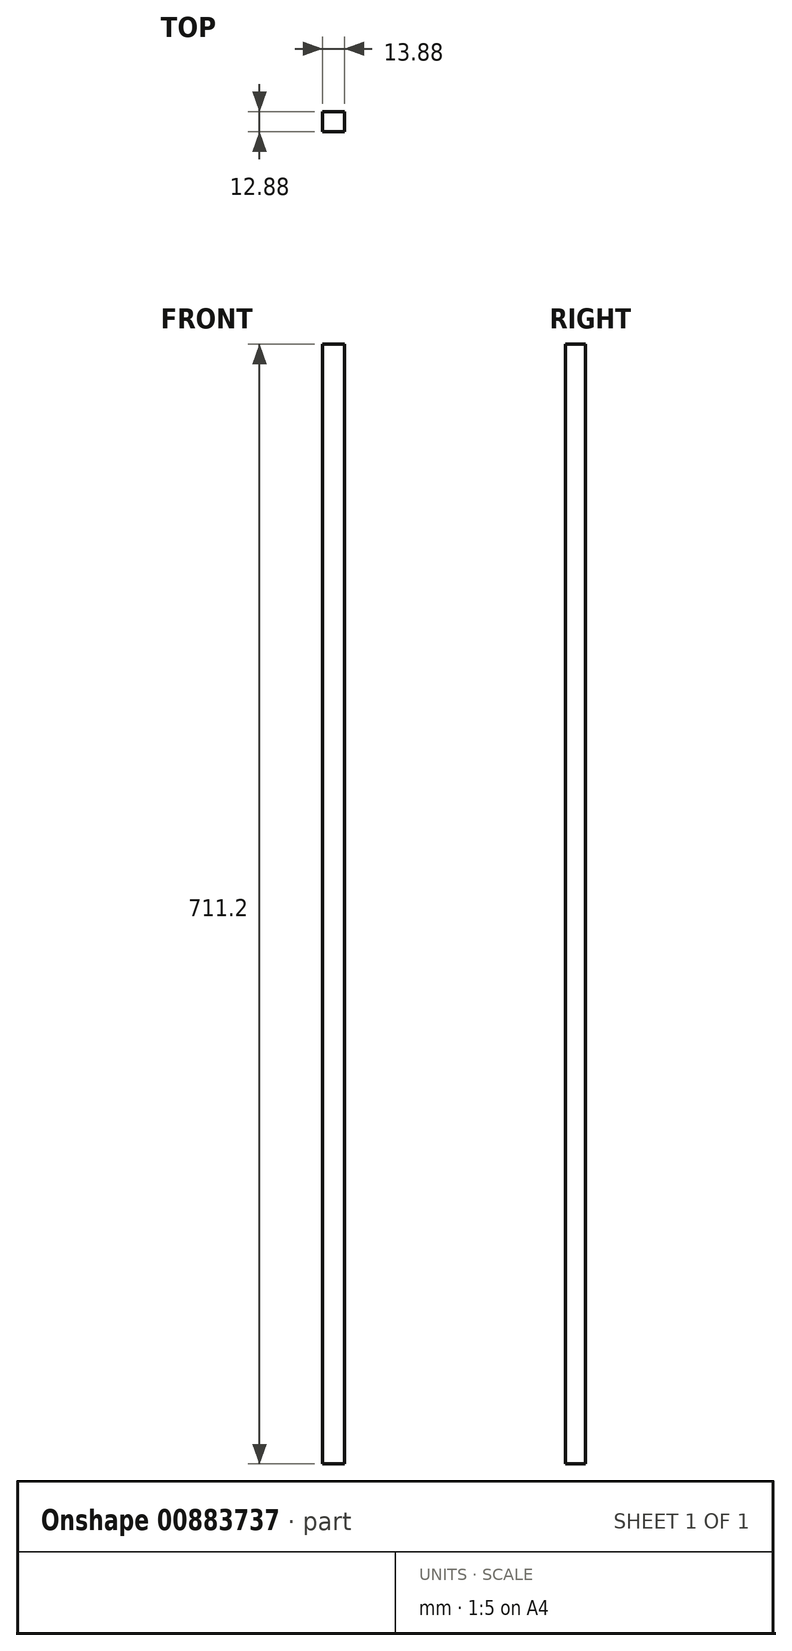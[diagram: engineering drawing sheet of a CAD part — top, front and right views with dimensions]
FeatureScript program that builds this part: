
annotation { "Feature Type Name" : "Feature", "Feature Type Description" : "" }
export const myFeature = defineFeature(function(context is Context, id is Id, definition is map)
    precondition{}
    {
        {
            var Q0;
            Q0=qCreatedBy(makeId("Top.planeOp"),FACE);
            var sketch = newSketch(context, id + "F0", { "sketchPlane" : qUnion([Q0])});
            skLineSegment(sketch, "E0.bottom", {"start": v(6.94, -6.44) * mm, "end": v(-6.94, -6.44) * mm});
            skLineSegment(sketch, "E0.top", {"start": v(6.94, 6.44) * mm, "end": v(-6.94, 6.44) * mm});
            skLineSegment(sketch, "E0.left", {"start": v(6.94, -6.44) * mm, "end": v(6.94, 6.44) * mm});
            skLineSegment(sketch, "E0.right", {"start": v(-6.94, -6.44) * mm, "end": v(-6.94, 6.44) * mm});
            skPoint(sketch, "E0.middle", {"position": v(0, 0) * mm});
            skSolve(sketch);
        }
        {
            var Q0;
            Q0=makeQuery(id+"F0.imprint","IMPRINT",FACE,{"disambiguationData":[TD([[makeQuery(id+"F0.imprint","IMPRINT",EDGE,{"derivedFrom":sQuery(id+"F0.wireOp",EDGE,"E0.bottom")}),-1.0]])]});
            extrude(context, id + "F1", {"entities" : qUnion([Q0]), "oppositeDirection" : true, "depth" : 711.2 * mm, "offsetDistance" : 25.4 * mm});
        }
    });
